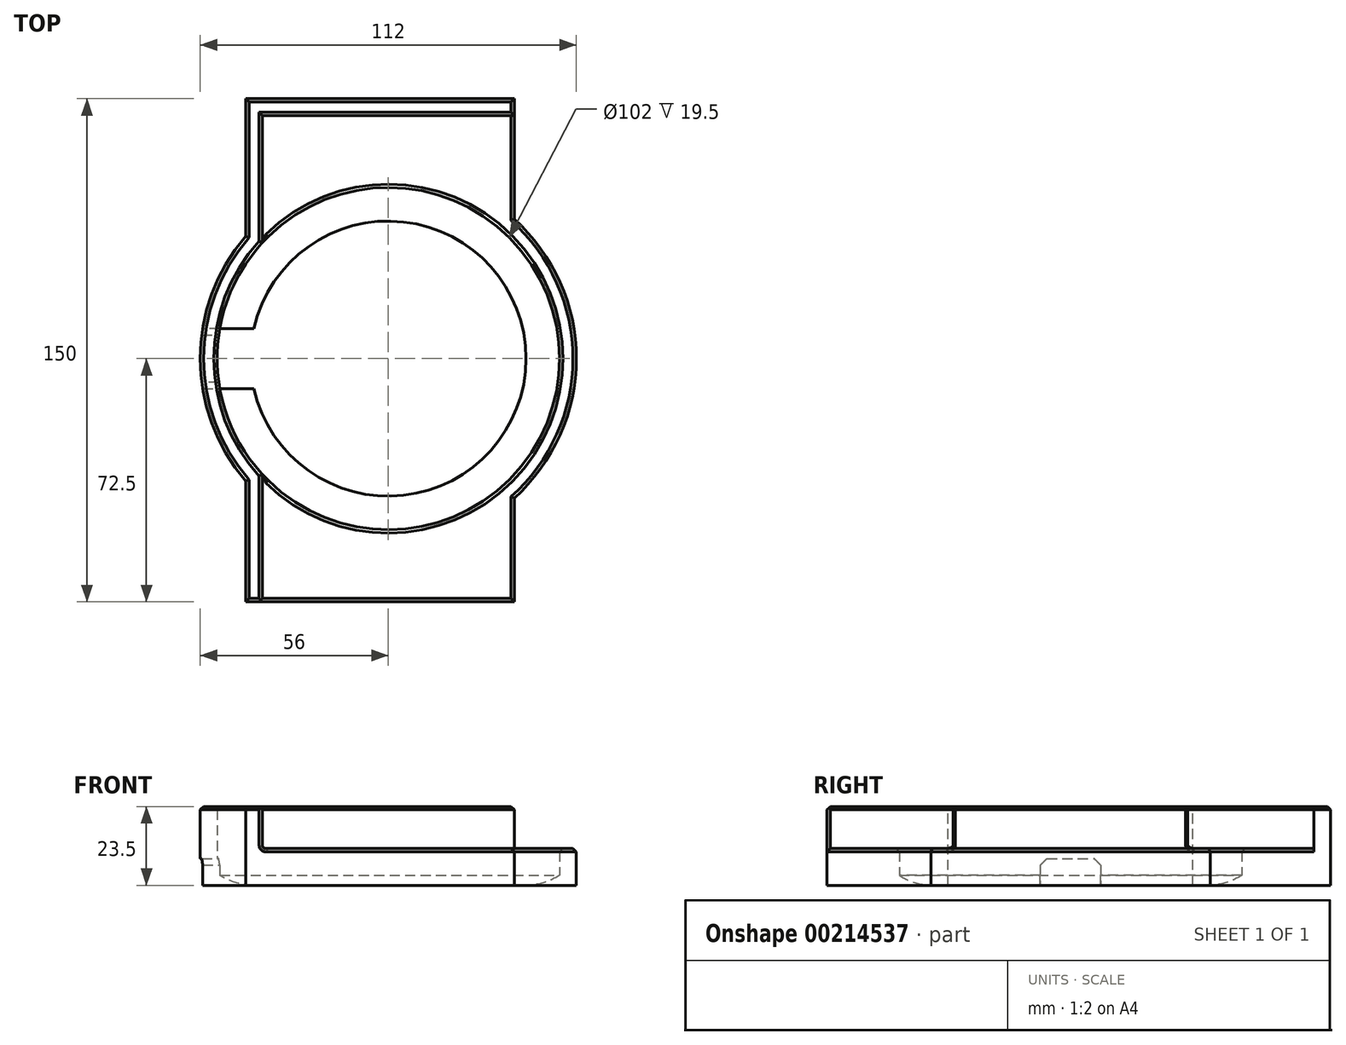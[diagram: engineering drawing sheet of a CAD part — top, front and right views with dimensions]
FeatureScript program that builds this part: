
annotation { "Feature Type Name" : "Feature", "Feature Type Description" : "" }
export const myFeature = defineFeature(function(context is Context, id is Id, definition is map)
    precondition{}
    {
        {
            var Q0;
            Q0=qCreatedBy(makeId("Top.planeOp"),FACE);
            var sketch = newSketch(context, id + "F0", { "sketchPlane" : qUnion([Q0])});
            skCircle(sketch, "E0", {"center": v(0, 0) * mm, "radius": 51 * mm});
            skCircle(sketch, "E1.0", {"center": v(0, 0) * mm, "radius": 56 * mm});
            skSolve(sketch);
        }
        {
            var Q0;
            Q0 = qSketchRegion(id + "F0", true);
            extrude(context, id + "F1", {"entities" : qUnion([Q0]), "depth" : 11 * mm});
        }
        {
            var Q0;
            Q0=makeQuery(id+"F1.opExtrude","CAP_FACE",FACE,{"disambiguationData":[OSD([sQuery(id+"F0.wireOp",EDGE,"E0"),sQuery(id+"F0.wireOp",EDGE,"E1.0")])],"isStart":true});
            var sketch = newSketch(context, id + "F2", { "sketchPlane" : qUnion([Q0])});
            skLineSegment(sketch, "E2.bottom", {"start": v(37.5, -72.5) * mm, "end": v(-37.5, -72.5) * mm});
            skLineSegment(sketch, "E2.top", {"start": v(37.5, 72.5) * mm, "end": v(-37.5, 72.5) * mm});
            skLineSegment(sketch, "E2.left", {"start": v(37.5, -72.5) * mm, "end": v(37.5, -41.6) * mm});
            skLineSegment(sketch, "E2.right", {"start": v(-37.5, -72.5) * mm, "end": v(-37.5, -41.6) * mm});
            skPoint(sketch, "E2.middle", {"position": v(0, 0) * mm});
            skArc(sketch, "E3.0", {"start": v(-37.5, -41.6) * mm, "mid": v(0, -56) * mm, "end": v(37.5, -41.6) * mm});
            skLineSegment(sketch, "E4.trimOffspring", {"start": v(-37.5, 41.6) * mm, "end": v(-37.5, 72.5) * mm});
            skLineSegment(sketch, "E5.trimOffspring", {"start": v(37.5, 41.6) * mm, "end": v(37.5, 72.5) * mm});
            skArc(sketch, "E6.trimOffspring", {"start": v(37.5, 41.6) * mm, "mid": v(0, 56) * mm, "end": v(-37.5, 41.6) * mm});
            skSolve(sketch);
        }
        {
            var Q0;
            Q0 = qSketchRegion(id + "F2", true);
            var Q1;
            Q1=makeQuery(id+"F1.opExtrude","CAP_FACE",FACE,{"disambiguationData":[OSD([sQuery(id+"F0.wireOp",EDGE,"E0"),sQuery(id+"F0.wireOp",EDGE,"E1.0")])],"isStart":false});
            extrude(context, id + "F3", {"entities" : qUnion([Q0]), "operationType" : NewBodyOperationType.ADD, "endBound" : BoundingType.UP_TO_SURFACE, "oppositeDirection" : true, "endBoundEntityFace" : qUnion([Q1]), "depth" : 25 * mm});
        }
        {
            var Q0;
            Q0=makeQuery(id+"F3.boolean.opBoolean","MERGE",FACE,{"derivedFrom":[makeQuery(id+"F1.opExtrude","CAP_FACE",FACE,{"disambiguationData":[OSD([sQuery(id+"F0.wireOp",EDGE,"E0"),sQuery(id+"F0.wireOp",EDGE,"E1.0")])],"isStart":false}),makeQuery(id+"F3.opExtrude","CAP_FACE",FACE,{"disambiguationData":[OSD([sQuery(id+"F2.wireOp",EDGE,"E2.bottom"),sQuery(id+"F2.wireOp",EDGE,"E2.left"),sQuery(id+"F2.wireOp",EDGE,"E2.right"),sQuery(id+"F2.wireOp",EDGE,"E3.0")])],"isStart":false}),makeQuery(id+"F3.opExtrude","CAP_FACE",FACE,{"disambiguationData":[OSD([sQuery(id+"F2.wireOp",EDGE,"E2.top"),sQuery(id+"F2.wireOp",EDGE,"E4.trimOffspring"),sQuery(id+"F2.wireOp",EDGE,"E5.trimOffspring"),sQuery(id+"F2.wireOp",EDGE,"E6.trimOffspring")])],"isStart":false})]});
            var sketch = newSketch(context, id + "F4", { "sketchPlane" : qUnion([Q0])});
            skLineSegment(sketch, "E7", {"start": v(-37.5, 72.5) * mm, "end": v(37.5, 72.5) * mm});
            skLineSegment(sketch, "E8", {"start": v(37.5, 72.5) * mm, "end": v(37.5, 77.5) * mm});
            skLineSegment(sketch, "E9", {"start": v(37.5, 77.5) * mm, "end": v(-42.5, 77.5) * mm});
            skLineSegment(sketch, "E10", {"start": v(-42.5, 77.5) * mm, "end": v(-42.5, 36.47) * mm});
            skLineSegment(sketch, "E11", {"start": v(-37.5, 72.5) * mm, "end": v(-37.5, 41.6) * mm});
            skLineSegment(sketch, "E12", {"start": v(-37.5, 72.5) * mm, "end": v(-42.5, 72.5) * mm, "construction": true});
            skLineSegment(sketch, "E13", {"start": v(-37.5, -72.5) * mm, "end": v(-37.5, -41.6) * mm});
            skLineSegment(sketch, "E14", {"start": v(-37.5, -72.5) * mm, "end": v(-42.5, -72.5) * mm});
            skLineSegment(sketch, "E15", {"start": v(-42.5, -72.5) * mm, "end": v(-42.5, -36.47) * mm});
            skLineSegment(sketch, "E16", {"start": v(-37.5, 41.6) * mm, "end": v(-37.5, 34.57) * mm});
            skLineSegment(sketch, "E17", {"start": v(-37.5, -41.6) * mm, "end": v(-37.5, -34.57) * mm});
            skArc(sketch, "E18", {"start": v(-37.5, 34.57) * mm, "mid": v(-51, 0) * mm, "end": v(-37.5, -34.57) * mm});
            skArc(sketch, "E19", {"start": v(-42.5, 36.47) * mm, "mid": v(-56, 0) * mm, "end": v(-42.5, -36.47) * mm});
            skLineSegment(sketch, "E20", {"start": v(-51, 0) * mm, "end": v(-56, 0) * mm, "construction": true});
            skSolve(sketch);
        }
        {
            var Q0;
            Q0 = qSketchRegion(id + "F4", true);
            var Q1;
            Q1=makeQuery(id+"F3.boolean.opBoolean","MERGE",FACE,{"derivedFrom":[makeQuery(id+"F1.opExtrude","CAP_FACE",FACE,{"disambiguationData":[OSD([sQuery(id+"F0.wireOp",EDGE,"E0"),sQuery(id+"F0.wireOp",EDGE,"E1.0")])],"isStart":true}),makeQuery(id+"F3.opExtrude","CAP_FACE",FACE,{"disambiguationData":[OSD([sQuery(id+"F2.wireOp",EDGE,"E2.bottom"),sQuery(id+"F2.wireOp",EDGE,"E2.left"),sQuery(id+"F2.wireOp",EDGE,"E2.right"),sQuery(id+"F2.wireOp",EDGE,"E3.0")])],"isStart":true}),makeQuery(id+"F3.opExtrude","CAP_FACE",FACE,{"disambiguationData":[OSD([sQuery(id+"F2.wireOp",EDGE,"E2.top"),sQuery(id+"F2.wireOp",EDGE,"E4.trimOffspring"),sQuery(id+"F2.wireOp",EDGE,"E5.trimOffspring"),sQuery(id+"F2.wireOp",EDGE,"E6.trimOffspring")])],"isStart":true})]});
            extrude(context, id + "F5", {"entities" : qUnion([Q0]), "operationType" : NewBodyOperationType.ADD, "endBound" : BoundingType.UP_TO_SURFACE, "oppositeDirection" : true, "endBoundEntityFace" : qUnion([Q1]), "depth" : 25 * mm, "hasSecondDirection" : true, "secondDirectionOppositeDirection" : false, "secondDirectionDepth" : 12.5 * mm});
        }
        {
            var Q0;
            Q0=qCreatedBy(makeId("Front.planeOp"),FACE);
            var sketch = newSketch(context, id + "F6", { "sketchPlane" : qUnion([Q0])});
            skLineSegment(sketch, "E21.0", {"start": v(-51, 0) * mm, "end": v(51, 0) * mm, "construction": true});
            skLineSegment(sketch, "E22", {"start": v(-51, 0) * mm, "end": v(-41, 0) * mm});
            skLineSegment(sketch, "E23", {"start": v(-51, 0) * mm, "end": v(-51, 3) * mm});
            skArc(sketch, "E24", {"start": v(-51, 3) * mm, "mid": v(-46.22, 0.77) * mm, "end": v(-41, 0) * mm});
            skSolve(sketch);
        }
        {
            var Q0;
            Q0=makeQuery(id+"F6.imprint","IMPRINT",FACE,{"disambiguationData":[TD([[makeQuery(id+"F6.imprint","IMPRINT",EDGE,{"derivedFrom":sQuery(id+"F6.wireOp",EDGE,"E22")}),1.0]])]});
            var Q1;
            Q1=makeQuery(id+"F1.opExtrude","CAP_EDGE",EDGE,{"disambiguationData":[OSD([sQuery(id+"F0.wireOp",EDGE,"E0")])],"isStart":true});
            sweep(context, id + "F7", {"operationType" : NewBodyOperationType.ADD, "profiles" : qUnion([Q0]), "path" : qUnion([Q1])});
        }
        {
            var Q0;
            Q0=qCreatedBy(makeId("Right.planeOp"),FACE);
            var sketch = newSketch(context, id + "F8", { "sketchPlane" : qUnion([Q0])});
            skLineSegment(sketch, "E25.0", {"start": v(-51, 3) * mm, "end": v(51, 3) * mm, "construction": true});
            skLineSegment(sketch, "E26", {"start": v(0, 3) * mm, "end": v(0, 23.5) * mm, "construction": true});
            skPoint(sketch, "E26.endSnap0", {"position": v(0, 3) * mm});
            skLineSegment(sketch, "E27", {"start": v(0, 3) * mm, "end": v(0, 0) * mm, "construction": true});
            skLineSegment(sketch, "E28.bottom", {"start": v(-9, 0) * mm, "end": v(9, 0) * mm});
            skLineSegment(sketch, "E28.top", {"start": v(-9, 8) * mm, "end": v(9, 8) * mm});
            skLineSegment(sketch, "E28.left", {"start": v(-9, 0) * mm, "end": v(-9, 8) * mm});
            skLineSegment(sketch, "E28.right", {"start": v(9, 0) * mm, "end": v(9, 8) * mm});
            skPoint(sketch, "E28.middle", {"position": v(0, 4) * mm});
            skSolve(sketch);
        }
        {
            var Q0;
            Q0 = qSketchRegion(id + "F8", true);
            extrude(context, id + "F9", {"entities" : qUnion([Q0]), "operationType" : NewBodyOperationType.REMOVE, "endBound" : BoundingType.THROUGH_ALL, "oppositeDirection" : true, "depth" : 25 * mm});
        }
        {
            var Q0;
            Q0=makeQuery(id+"F3.opExtrude","CAP_EDGE",EDGE,{"disambiguationData":[OSD([sQuery(id+"F2.wireOp",EDGE,"E2.bottom")])],"isStart":false});
            var Q1;
            Q1=makeQuery(id+"F5.boolean.opBoolean","INTERSECT",EDGE,{"derivedFrom":[makeQuery(id+"F3.boolean.opBoolean","MERGE",FACE,{"derivedFrom":[makeQuery(id+"F1.opExtrude","CAP_FACE",FACE,{"disambiguationData":[OSD([sQuery(id+"F0.wireOp",EDGE,"E0"),sQuery(id+"F0.wireOp",EDGE,"E1.0")])],"isStart":false}),makeQuery(id+"F3.opExtrude","CAP_FACE",FACE,{"disambiguationData":[OSD([sQuery(id+"F2.wireOp",EDGE,"E2.bottom"),sQuery(id+"F2.wireOp",EDGE,"E2.left"),sQuery(id+"F2.wireOp",EDGE,"E2.right"),sQuery(id+"F2.wireOp",EDGE,"E3.0")])],"isStart":false}),makeQuery(id+"F3.opExtrude","CAP_FACE",FACE,{"disambiguationData":[OSD([sQuery(id+"F2.wireOp",EDGE,"E2.top"),sQuery(id+"F2.wireOp",EDGE,"E4.trimOffspring"),sQuery(id+"F2.wireOp",EDGE,"E5.trimOffspring"),sQuery(id+"F2.wireOp",EDGE,"E6.trimOffspring")])],"isStart":false})]}),makeQuery(id+"F5.opExtrude","SWEPT_FACE",FACE,{"disambiguationData":[OSD([sQuery(id+"F4.wireOp",EDGE,"E11"),sQuery(id+"F4.wireOp",EDGE,"E16")])]})]});
            var Q2;
            Q2=makeQuery(id+"F5.boolean.opBoolean","INTERSECT",EDGE,{"derivedFrom":[makeQuery(id+"F3.boolean.opBoolean","MERGE",FACE,{"derivedFrom":[makeQuery(id+"F1.opExtrude","CAP_FACE",FACE,{"disambiguationData":[OSD([sQuery(id+"F0.wireOp",EDGE,"E0"),sQuery(id+"F0.wireOp",EDGE,"E1.0")])],"isStart":false}),makeQuery(id+"F3.opExtrude","CAP_FACE",FACE,{"disambiguationData":[OSD([sQuery(id+"F2.wireOp",EDGE,"E2.bottom"),sQuery(id+"F2.wireOp",EDGE,"E2.left"),sQuery(id+"F2.wireOp",EDGE,"E2.right"),sQuery(id+"F2.wireOp",EDGE,"E3.0")])],"isStart":false}),makeQuery(id+"F3.opExtrude","CAP_FACE",FACE,{"disambiguationData":[OSD([sQuery(id+"F2.wireOp",EDGE,"E2.top"),sQuery(id+"F2.wireOp",EDGE,"E4.trimOffspring"),sQuery(id+"F2.wireOp",EDGE,"E5.trimOffspring"),sQuery(id+"F2.wireOp",EDGE,"E6.trimOffspring")])],"isStart":false})]}),makeQuery(id+"F5.opExtrude","SWEPT_FACE",FACE,{"disambiguationData":[OSD([sQuery(id+"F4.wireOp",EDGE,"E13"),sQuery(id+"F4.wireOp",EDGE,"E17")])]})]});
            fillet(context, id + "F10", {"entities" : qUnion([Q0, Q1, Q2]), "radius" : 1 * mm, "tangentPropagation" : true, "allowEdgeOverflow" : false});
        }
        {
            var Q0;
            Q0=makeQuery(id+"F5.opExtrude","CAP_FACE",FACE,{"disambiguationData":[OSD([sQuery(id+"F4.wireOp",EDGE,"E7"),sQuery(id+"F4.wireOp",EDGE,"E8"),sQuery(id+"F4.wireOp",EDGE,"E9"),sQuery(id+"F4.wireOp",EDGE,"E10"),sQuery(id+"F4.wireOp",EDGE,"E11"),sQuery(id+"F4.wireOp",EDGE,"E13"),sQuery(id+"F4.wireOp",EDGE,"E14"),sQuery(id+"F4.wireOp",EDGE,"E15"),sQuery(id+"F4.wireOp",EDGE,"E16"),sQuery(id+"F4.wireOp",EDGE,"E17"),sQuery(id+"F4.wireOp",EDGE,"E18"),sQuery(id+"F4.wireOp",EDGE,"E19")])],"isStart":true});
            chamfer(context, id + "F11", {"entities" : qUnion([Q0]), "width" : 1 * mm, "tangentPropagation" : true});
        }
        {
            var Q0;
            Q0=makeQuery(id+"F3.opExtrude","CAP_EDGE",EDGE,{"disambiguationData":[OSD([sQuery(id+"F2.wireOp",EDGE,"E2.top")])],"isStart":false});
            var Q1;
            Q1=makeQuery(id+"F3.opExtrude","CAP_EDGE",EDGE,{"disambiguationData":[OSD([sQuery(id+"F2.wireOp",EDGE,"E5.trimOffspring")])],"isStart":false});
            var Q2;
            {var subQ0=sQuery(id+"F2.wireOp",EDGE,"E2.left");var subQ1=sQuery(id+"F0.wireOp",EDGE,"E1.0");Q2=makeQuery(id+"F3.boolean.opBoolean","SPLIT",EDGE,{"disambiguationData":[TD([makeQuery(id+"F3.opExtrude","SWEPT_FACE",FACE,{"disambiguationData":[OSD([subQ0])]})])],"derivedFrom":makeQuery(id+"F1.opExtrude","CAP_EDGE",EDGE,{"disambiguationData":[OSD([subQ1])],"isStart":false})});}
            var Q3;
            Q3=makeQuery(id+"F3.opExtrude","CAP_EDGE",EDGE,{"disambiguationData":[OSD([sQuery(id+"F2.wireOp",EDGE,"E2.left")])],"isStart":false});
            chamfer(context, id + "F12", {"entities" : qUnion([Q0, Q1, Q2, Q3]), "width" : 1 * mm, "tangentPropagation" : true});
        }
        {
            var Q0;
            Q0=makeQuery(id+"F1.opExtrude","CAP_EDGE",EDGE,{"disambiguationData":[OSD([sQuery(id+"F0.wireOp",EDGE,"E0")])],"isStart":false});
            chamfer(context, id + "F13", {"entities" : qUnion([Q0]), "width" : 1 * mm, "tangentPropagation" : true});
        }
        {
            var Q0;
            Q0=makeQuery(id+"F9.boolean.opBoolean","COPY",EDGE,{"derivedFrom":makeQuery(id+"F9.opExtrude","SWEPT_EDGE",EDGE,{"disambiguationData":[OSD([sQuery(id+"F8.wireOp",EDGE,"E28.top"),sQuery(id+"F8.wireOp",EDGE,"E28.right")])]})});
            var Q1;
            Q1=makeQuery(id+"F9.boolean.opBoolean","COPY",EDGE,{"derivedFrom":makeQuery(id+"F9.opExtrude","SWEPT_EDGE",EDGE,{"disambiguationData":[OSD([sQuery(id+"F8.wireOp",EDGE,"E28.top"),sQuery(id+"F8.wireOp",EDGE,"E28.left")])]})});
            chamfer(context, id + "F14", {"entities" : qUnion([Q0, Q1]), "width" : 2 * mm, "tangentPropagation" : true});
        }
    });
